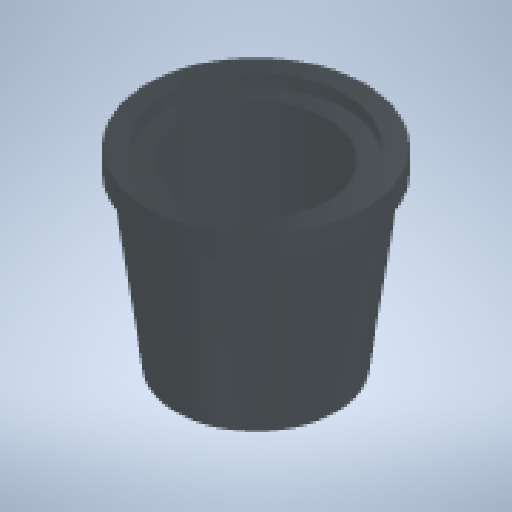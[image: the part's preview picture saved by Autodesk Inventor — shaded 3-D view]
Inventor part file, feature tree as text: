
AUTODESK INVENTOR PART (.ipt)
format: ipt  version: 2023 (Build 270158000, 158)  size: 154,112 bytes
history: native  units: mm
features: revolve x1, sketch x1
ambient origin geometry x8: Origin, YZ Plane, XZ Plane, XY Plane, X Axis, Y Axis, Z Axis, Center Point
bodies: Solid1 (feature_tree)
feature tree (2):
  revolve  "Revolution1"  [1 undecoded]
  sketch  "Sketch1"  dims[d0=90.0deg d1=36.5mm d2=24.0mm d3=30.0mm d4=2.0mm d5=1.0mm d6=30.0mm d7=27.0mm d8=2.0mm]
note: 1 required parameter value undecoded (feature->parameter linkage not recoverable at this tier; creation-order binding heuristic only, values carry confidence <= 0.55)
